# Revit family: BE_99415_de_DE
name_source: partatom
category: Leuchten
units: mm (PartAtom-declared; Revit-internal decimal feet)

## family parameters
Basisbauteil = Fläche
Beim Laden mit Abzugskörper schneiden = Ja
Bemaßung runder Anschluss = Durchmesser verwenden
Gemeinsam genutzt = Ja
Lichtquelle = Nein
Raumberechnungspunkt = Ja
Teiletyp = Normal

## types (1)
- BEGA_99415_K3
    AC/DC = AC
    Aktualisierung = 2022-05-20T04:00:08
    Anschlussleitung = 4.0 m H07RN8-F 3 G 1²
    BEGA_Dummy = Nein
    BEGA_IES = Ja
    BEGA_Intern = Ja
    BEGA_Intern_Konstruktion = Ja
    BEGA_Intern_an = Ja
    BEGA_Intern_aus = Ja
    Befestigungsabstand = 45 mm
    Befestigungsbohrung = Ø 7 mm
    Beschreibung = Unterwasserscheinwerfer
    Beschreibung_Sonderanfertigung = Hier können Sie Informationen zur Sonderanfertigung eintragen.
    Bestellnummer = 99415K3
    CE_Konformität = ja
    D_Breite = 0 mm  [stored 0 ft]
    D_Durchmesser = 0 mm  [stored 0 ft]
    D_Höhe = 0 mm  [stored 0 ft]
    D_Länge = 0 mm  [stored 0 ft]
    Energieeffizienzklasse = LED A++ - A
    Farbtemperatur = 3000 K
    Farbwiedergabeindex = CRI > 80
    Frequenz = 50-60 Hz
    Gewicht = 4.15 kg
    Hersteller = BEGA
    Höhe_Platte = -10 mm  [stored -0.0328084 ft]
    LED_Modulbezeichnung = LED-1165/830
    Lampe = LED 15.5 W
    Lampenlichtstrom = 3010 lm
    Lebensdauerkriterien = L70B50 @ 25 °C = 200000 h
    Leuchtenlichtstrom = 2169 lm
    Logo = BEGA_Logo.png
    Material_06 = BEGA_Oberfläche_Edelstahl_gebürstet
    Material_09 = BEGA_Glas_klar
    Material_16 = BEGA_Leuchtmedium_glanz
    Material_17 = BEGA_Reflektor
    Material_19 = BEGA_Dummy_matt
    Material_20 = BEGA_Platte_Weiss
    Modell = 99415K3
    Produktdatenblatt = https://cdn.bega.com
    Schutzart = IP 68...20m
    Schutzklasse = I
    Sonderanfertigung = Nein
    Spannung = 220-240 V
    Typenbild = 99415.png
    URL = https://www.bega.com
    Umgebungstemperatur = 25 °C
    Vorgabe-Ansicht = 0 mm  [stored 0 ft]

note: [stored X ft] marks values corroborated as IEEE doubles in the binary element streams (Revit-internal decimal feet)

## geometry (parser evidence)
native form markers: Blend x2, Sweep x7
no freeform markers — native parametric forms only
